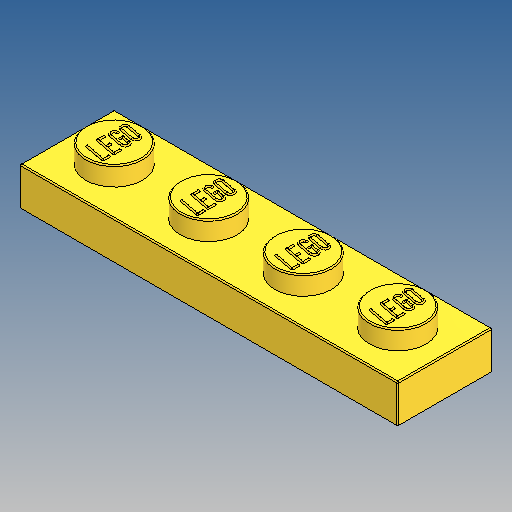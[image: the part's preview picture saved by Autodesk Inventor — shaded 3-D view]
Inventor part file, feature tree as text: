
AUTODESK INVENTOR PART (.ipt)
format: ipt  version: 2025 (Build 290162010, 162A)  size: 1,349,632 bytes
history: native  units: in
note: dims shown in document units (in); Inventor stores cm internally (conversion verified against a paired STEP export)
features: extrude x4, sketch x4, fillet x2, pattern_linear x2, other x1
ambient origin geometry x8: Origin, YZ Plane, XZ Plane, XY Plane, X Axis, Y Axis, Z Axis, Center Point
bodies: Solid1 (feature_tree)
feature tree (13):
  extrude  "Extrusion1"  Depth=0.315in
  extrude  "Extrusion4"  Depth=0.063in
  other  "LEGO:1"
  fillet  "Fillet2"  Radius=0.063in
  pattern_linear  "Rectangular Pattern1"  Spacing1=0.189in  [1 undecoded]
  sketch  "Sketch3"  dims[d4=0.126in d5=0.0in d7=0.0591in d8=0.063in d11=0.063in d12=0.0in]
  extrude  "Extrusion2"  Depth=0.063in
  extrude  "Extrusion5"  Depth=0.189in
  pattern_linear  "Rectangular Pattern2"  Spacing1=0.1575in  [1 undecoded]
  fillet  "Fillet1"  Radius=0.1575in
  sketch  "Sketch2"  dims[d0=1.2598in d1=0.315in]
  sketch  "Sketch9"  dims[d22=0.0039in]
  sketch  "Sketch10"  dims[d60=0.2564in d61=0.189in d62=0.063in d63=0.189in d64=0.1575in d65=0.1575in d66=0.063in d67=0.0in d68=0.0039in d69=1.5748in d71=0.315in d72=0.3937in d74=0.315in d75=0.315in d76=0.315in d77=0.0709in d78=0.0in d79=1.1811in d81=0.315in d82=0.3937in d84=0.315in d85=0.126in d86=0.0in d87=0.0in d88=0.0in d89=0.0in d90=0.0in d91=0.0079in d92=0.0732in d93=0.0281in d94=0.035in d95=0.0079in d96=0.0139in d97=0.0281in d98=0.035in d99=0.0281in d100=0.0159in d101=0.0177in d102=0.035in d103=0.5428in]
note: 2 required parameter values undecoded (feature->parameter linkage not recoverable at this tier; creation-order binding heuristic only, values carry confidence <= 0.55)
